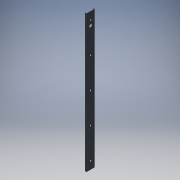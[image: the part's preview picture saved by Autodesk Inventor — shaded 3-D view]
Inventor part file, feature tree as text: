
AUTODESK INVENTOR PART (.ipt)
format: ipt  version: 2016 (Build 200138000, 138)  size: 164,864 bytes
history: native  units: mm
features: other x14, sketch x7, extrude x6, hole x1
ambient origin geometry x8: Origin, YZ Plane, XZ Plane, XY Plane, X Axis, Y Axis, Z Axis, Center Point
bodies: Solid1 (feature_tree)
feature tree (28):
  extrude  "Extrusion1"  Depth=1.0mm TaperAngle=0.0deg
  hole  "Hole1"  [1 undecoded]
  extrude  "Extrusion2"  Depth=1.0mm TaperAngle=0.0deg
  extrude  "Extrusion3"  [1 undecoded]
  extrude  "Extrusion4"  [1 undecoded]
  extrude  "Extrusion5"  [1 undecoded]
  extrude  "Extrusion6"  [1 undecoded]
  other  "to_body_XY"
  other  "to_body_YZ"
  other  "to_body_ZX"
  other  "to_body_X"
  other  "to_body_Y"
  other  "to_body_Z"
  other  "to_body_Center"
  other  "to_slider_XY"
  other  "to_slider_YZ"
  other  "to_slider_ZX"
  other  "to_slider_X"
  other  "to_slider_Y"
  other  "to_slider_Z"
  other  "to_slider_Center"
  sketch  "Sketch_1"  dims[d0=457.2mm d1=0.0mm]
  sketch  "Sketch2"  dims[d2=9.5mm d3=6.0mm d4=4.0mm d5=2.0mm d6=90.0deg d7=1.0mm d8=0.0mm d9=1.0mm d10=0.0mm]
  sketch  "Sketch_5"  dims[d11=1.0mm d12=0.0mm d13=1.0mm d14=0.0mm]
  sketch  "Sketch_6"  dims[d15=1.0mm d16=0.0mm d17=1.0mm d18=0.0mm]
  sketch  "Sketch_7"
  sketch  "Sketch_8"
  sketch  "Sketch_9"
note: 5 required parameter values undecoded (feature->parameter linkage not recoverable at this tier; creation-order binding heuristic only, values carry confidence <= 0.55)
